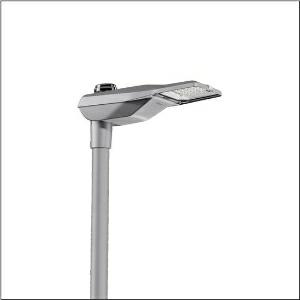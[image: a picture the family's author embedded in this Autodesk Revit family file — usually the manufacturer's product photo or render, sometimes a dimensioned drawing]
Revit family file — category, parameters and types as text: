
# Revit family: streetlight_sl_21_micro___st1_0a_5xe5d67n08db_977e
name_source: partatom
category: Lighting Fixtures
units: mm (PartAtom-declared; Revit-internal decimal feet)

## family parameters
Cut with Voids When Loaded = No
Host = Face
Light Source = No
Part Type = Normal
Room Calculation Point = No
Round Connector Dimension = Use Diameter
Shared = No

## types (1)
- --- (1 x LED, 4580 lm, 39.1 W, 2700K)
    Apparent Load = 39 VA
    CIE Flux Codes = 37 72 97 100 100
    Color Rendering = 70
    Color Temperature = 2700K
    Default Elevation = 1800 mm
    Description = Streetlight SL 21 micro, mast luminaire, primary light control with lens, of PMMA, primary optical cover: cover, of toughened safety glass, transparent, light distribution: ST1.0a, light emission: direct distribution, primary light characteristic: asymmetric, installation type: post-top, LED, 3G 1.5mm², High Power LED, rated luminous flux: 4.580lm, luminous efficacy: 117lm/W, light colour: 727, colour temperature: 2700K, control gear: NEMA (7pin), control: overheat protection, pre-setting: linear dimming characteristic, constant luminous flux control, time-dependent luminous flux control, flexible luminous flux parameterisation, mains connection: 230..240V, AC, 50/60Hz, connection cable pre-assembled, cable length: 6,5m, wiring characteristics: H07RN-F, start of lifetime: 39W, end of service life: 41W, reduction: 18W, luminaire housing, of diecast aluminium (EN AC-44300), powder-coated, Siteco® metallic grey (DB 702S), corrosivity category C5 mid according to DIN EN ISO 12944, multi-level sealing system, sealing non-destructively replaceable, inclination adjustable: 0°, 5°, 10°, 15°, length: 528mm, width: 235mm, height: 110mm, spigot size: 76/60mm (post-top), mounting height: 4..8m, protection rating (complete): IP66, insulation class (complete): insulation class I (protective earthing), certification: CE, ENEC, ENEC+, VDE, impact resistance: IK10, permissible operating ambient temperature for outdoor applications: -40..+50°C, standard-compliant lighting for roads and squares, packaging unit: 1 piece

Light Distribution: ST1.0a
    Height = 110 mm
    Lamp = 1 x LED
    Lamp Light Flux = 4580 lm
    Lamp Power = 39.1 W
    Lamp count = 1
    Length = 528 mm
    Luminous efficacy = 117 lm/W
    Manufacturer = Siteco
    ModVariant = No
    Model = 5XE5D67N08DB
    Number of Poles = 1
    OnlyDefault = Yes
    Power Factor = 1
    Product Name = Streetlight SL 21 micro | ST1.0a
    Product group = mast luminaire | pylon top
    ProductGroupID = 6100
    Protection Class = Protection class I
    Protection Degree = IP 66
    RLX_Detail_Level = 1
    RLX_Emergency_Light_Flux = 0 lm
    RLX_Emergency_Type = 0
    RLX_Emergency_Type_DB = No
    RlxData = <blob elided: 98437 chars, md5=c1f83f2d>
    Socket = socket
    Standby Power = 0 W
    System Light Flux = 4580 lm
    System Power = 39 W
    Type Comments = factory setting: luminous flux: 100 % | dim-lin: 254 | 765 mA
    Type Image = l_1294375.jpg
    URL = http://relux.com
    VarID = @adj_136400
    Voltage = 0 V
    Weight = 0.00 kg
    Width = 235 mm

## geometry (parser evidence)
native form markers: Blend x4, Sweep x10
no freeform markers — native parametric forms only
